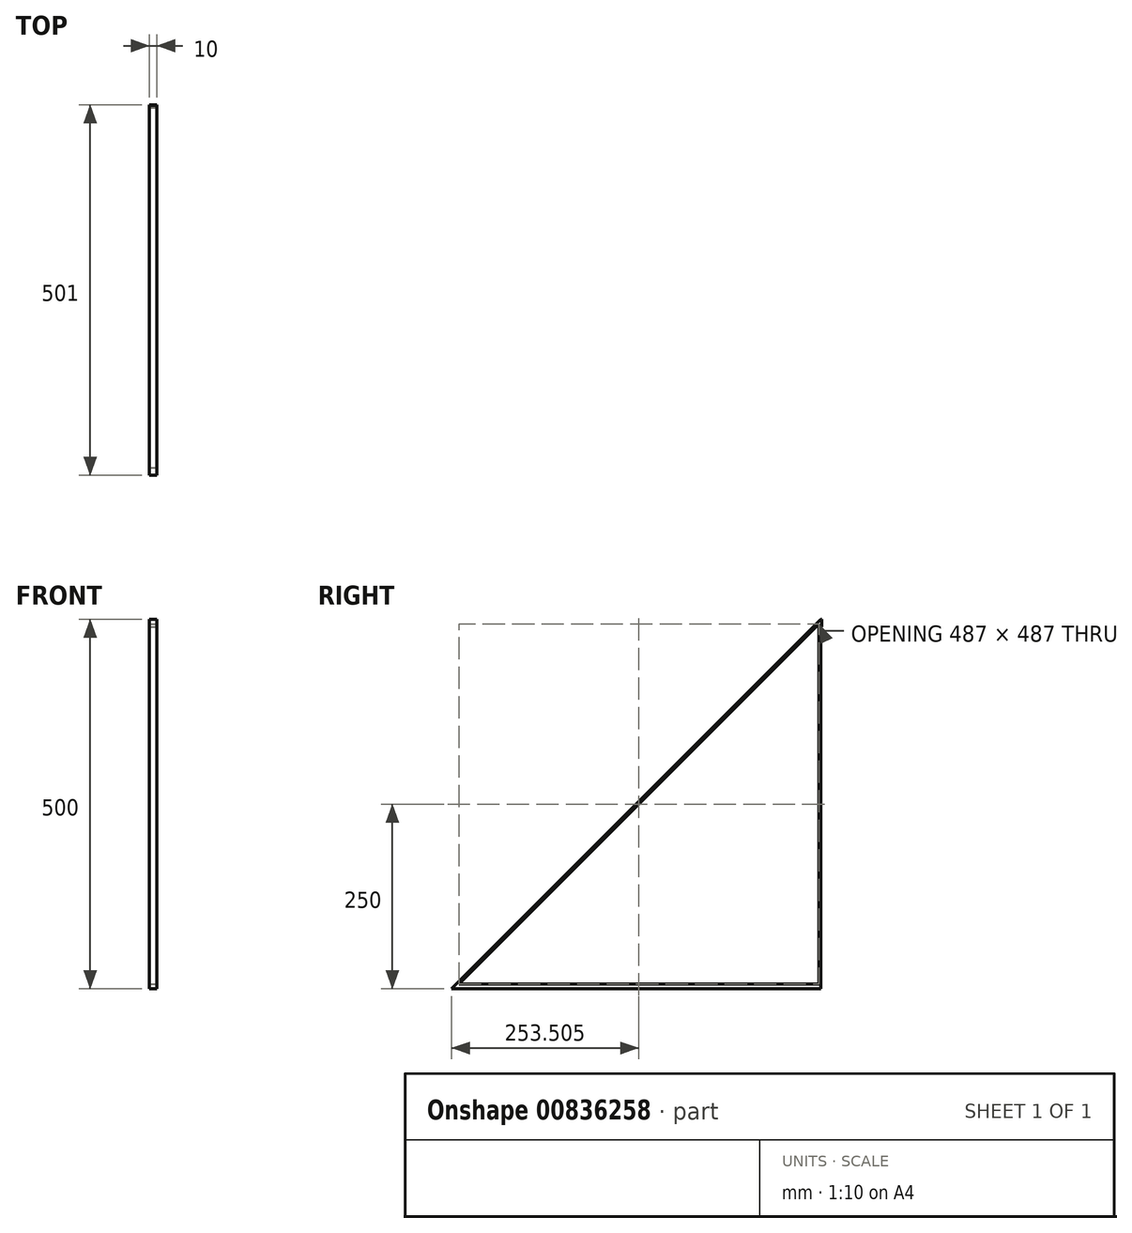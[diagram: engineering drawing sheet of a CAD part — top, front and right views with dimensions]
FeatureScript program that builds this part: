
annotation { "Feature Type Name" : "Feature", "Feature Type Description" : "" }
export const myFeature = defineFeature(function(context is Context, id is Id, definition is map)
    precondition{}
    {
        {
            var Q0;
            Q0=qCreatedBy(makeId("Top.planeOp"),FACE);
            var sketch = newSketch(context, id + "F0", { "sketchPlane" : qUnion([Q0])});
            skLineSegment(sketch, "E0", {"start": v(-17.1, 464.33) * mm, "end": v(-7.1, 464.33) * mm});
            skLineSegment(sketch, "E1", {"start": v(-7.1, 464.33) * mm, "end": v(-7.1, -35.67) * mm});
            skLineSegment(sketch, "E2", {"start": v(-7.1, -35.67) * mm, "end": v(-17.1, -35.67) * mm});
            skLineSegment(sketch, "E3", {"start": v(-17.1, -35.67) * mm, "end": v(-17.1, 464.33) * mm});
            skSolve(sketch);
        }
        {
            var Q0;
            Q0 = qSketchRegion(id + "F0", true);
            extrude(context, id + "F1", {"entities" : qUnion([Q0]), "depth" : 500 * mm, "offsetDistance" : 25 * mm});
        }
        {
            var Q0;
            Q0=makeQuery(id+"F1.opExtrude","SWEPT_FACE",FACE,{"disambiguationData":[OSD([sQuery(id+"F0.wireOp",EDGE,"E3")])]});
            var sketch = newSketch(context, id + "F2", { "sketchPlane" : qUnion([Q0])});
            skLineSegment(sketch, "E4", {"start": v(-464.33, 500) * mm, "end": v(35.67, 0) * mm});
            skSolve(sketch);
        }
        {
            var Q0;
            Q0=makeQuery(id+"F2.imprint","IMPRINT",FACE,{"disambiguationData":[TD([[makeQuery(id+"F2.imprint","IMPRINT",EDGE,{"derivedFrom":sQuery(id+"F2.wireOp",EDGE,"E4")}),1.0]])]});
            extrude(context, id + "F3", {"entities" : qUnion([Q0]), "operationType" : NewBodyOperationType.REMOVE, "oppositeDirection" : true, "depth" : 10 * mm, "offsetDistance" : 25 * mm});
        }
        {
            var Q0;
            Q0=makeQuery(id+"F1.opExtrude","SWEPT_FACE",FACE,{"disambiguationData":[OSD([sQuery(id+"F0.wireOp",EDGE,"E1")])]});
            var sketch = newSketch(context, id + "F4", { "sketchPlane" : qUnion([Q0])});
            skPoint(sketch, "E5", {"position": v(461.33, 6.5) * mm});
            skPoint(sketch, "E6", {"position": v(-25.67, 6.5) * mm});
            skPoint(sketch, "E7", {"position": v(461.33, 493.5) * mm});
            skLineSegment(sketch, "E8", {"start": v(-25.67, 6.5) * mm, "end": v(461.33, 6.5) * mm});
            skLineSegment(sketch, "E9", {"start": v(461.33, 6.5) * mm, "end": v(461.33, 493.5) * mm});
            skLineSegment(sketch, "E10", {"start": v(-25.67, 6.5) * mm, "end": v(461.33, 493.5) * mm});
            skSolve(sketch);
        }
        {
            var Q0;
            Q0=makeQuery(id+"F4.imprint","IMPRINT",FACE,{"disambiguationData":[TD([[makeQuery(id+"F4.imprint","IMPRINT",EDGE,{"derivedFrom":sQuery(id+"F4.wireOp",EDGE,"E8")}),1.0]])]});
            extrude(context, id + "F5", {"entities" : qUnion([Q0]), "operationType" : NewBodyOperationType.REMOVE, "oppositeDirection" : true, "depth" : 10 * mm, "offsetDistance" : 25 * mm});
        }
        {
            var Q0;
            Q0=makeQuery(id+"F1.opExtrude","SWEPT_FACE",FACE,{"disambiguationData":[OSD([sQuery(id+"F0.wireOp",EDGE,"E0")])]});
            var sketch = newSketch(context, id + "F6", { "sketchPlane" : qUnion([Q0])});
            skLineSegment(sketch, "E11.bottom", {"start": v(17.1, 500) * mm, "end": v(7.1, 500) * mm});
            skLineSegment(sketch, "E11.top", {"start": v(17.1, 490) * mm, "end": v(7.1, 490) * mm});
            skLineSegment(sketch, "E11.left", {"start": v(17.1, 500) * mm, "end": v(17.1, 490) * mm});
            skLineSegment(sketch, "E11.right", {"start": v(7.1, 500) * mm, "end": v(7.1, 490) * mm});
            skPoint(sketch, "E11.middle", {"position": v(12.1, 495) * mm});
            skSolve(sketch);
        }
        {
            var Q0;
            Q0=makeQuery(id+"F6.imprint","IMPRINT",FACE,{"disambiguationData":[TD([[makeQuery(id+"F6.imprint","IMPRINT",EDGE,{"derivedFrom":sQuery(id+"F6.wireOp",EDGE,"E11.bottom")}),1.0]])]});
            extrude(context, id + "F7", {"entities" : qUnion([Q0]), "operationType" : NewBodyOperationType.ADD, "depth" : 1 * mm, "offsetDistance" : 25 * mm});
        }
    });
